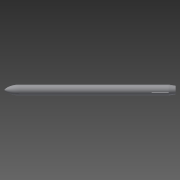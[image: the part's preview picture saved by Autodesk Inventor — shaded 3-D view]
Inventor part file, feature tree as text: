
AUTODESK INVENTOR PART (.ipt)
format: ipt  version: 2014 SP1 (Build 180222100, 222)  size: 218,624 bytes
history: native  units: mm
features: plane x8, sketch x8, extrude x4, pattern_circular x2, revolve x2, shell x1, fillet x1, projected_geometry x1
ambient origin geometry x8: Origin, YZ Plane, XZ Plane, XY Plane, X Axis, Y Axis, Z Axis, Center Point
bodies: Solid1 (feature_tree)
feature tree (27):
  extrude  "Extrusion1"  Depth=1200.0mm TaperAngle=0.0deg
  plane  "Work Plane1"
  plane  "Work Plane2"
  extrude  "Extrusion4"  Depth=5.0mm
  pattern_circular  "Circular Pattern2"  Count=2 Angle=360.0deg
  sketch  "Sketch5"  dims[d28=25.0mm d29=0.0mm d30=20.0mm d31=360.0deg]
  plane  "Work Plane3"
  plane  "Work Plane4"
  extrude  "Extrusion5"  Depth=35.0mm
  pattern_circular  "Circular Pattern3"  Count=11  [1 undecoded]
  plane  "Work Plane5"
  extrude  "Extrusion6"  Depth=10.0mm TaperAngle=360.0deg
  plane  "Work Plane6"
  revolve  "Revolution2"  [1 undecoded]
  plane  "Work Plane7"
  revolve  "Revolution3"  [1 undecoded]
  shell  "Shell1"  Thickness=450.0mm
  fillet  "Fillet2"  [1 undecoded]
  plane  "Work Plane8"
  sketch  "Sketch11"  dims[d53=5.0mm d54=10.0mm d55=0.0mm d62=450.0mm d63=0.0mm d67=90.0deg d68=0.0mm d69=28.0mm d70=90.0deg d72=3.0mm d73=1.5mm d74=0.0mm]
  sketch  "Sketch1"  dims[d0=70.0mm d1=1200.0mm d2=0.0mm]
  sketch  "Sketch4"  dims[d10=35.0mm d21=35.0mm d26=5.0mm]
  sketch  "Sketch7"  dims[d33=0.0mm d39=35.0mm]
  sketch  "Sketch8"  dims[d41=5.0mm d42=110.0mm]
  sketch  "Sketch9"  dims[d43=10.0mm d44=0.0mm d45=30.0mm d46=360.0deg]
  sketch  "Sketch10"  dims[d49=-35.0mm d52=36.0mm]
  projected_geometry  "Projected Loop1"
note: 4 required parameter values undecoded (feature->parameter linkage not recoverable at this tier; creation-order binding heuristic only, values carry confidence <= 0.55)